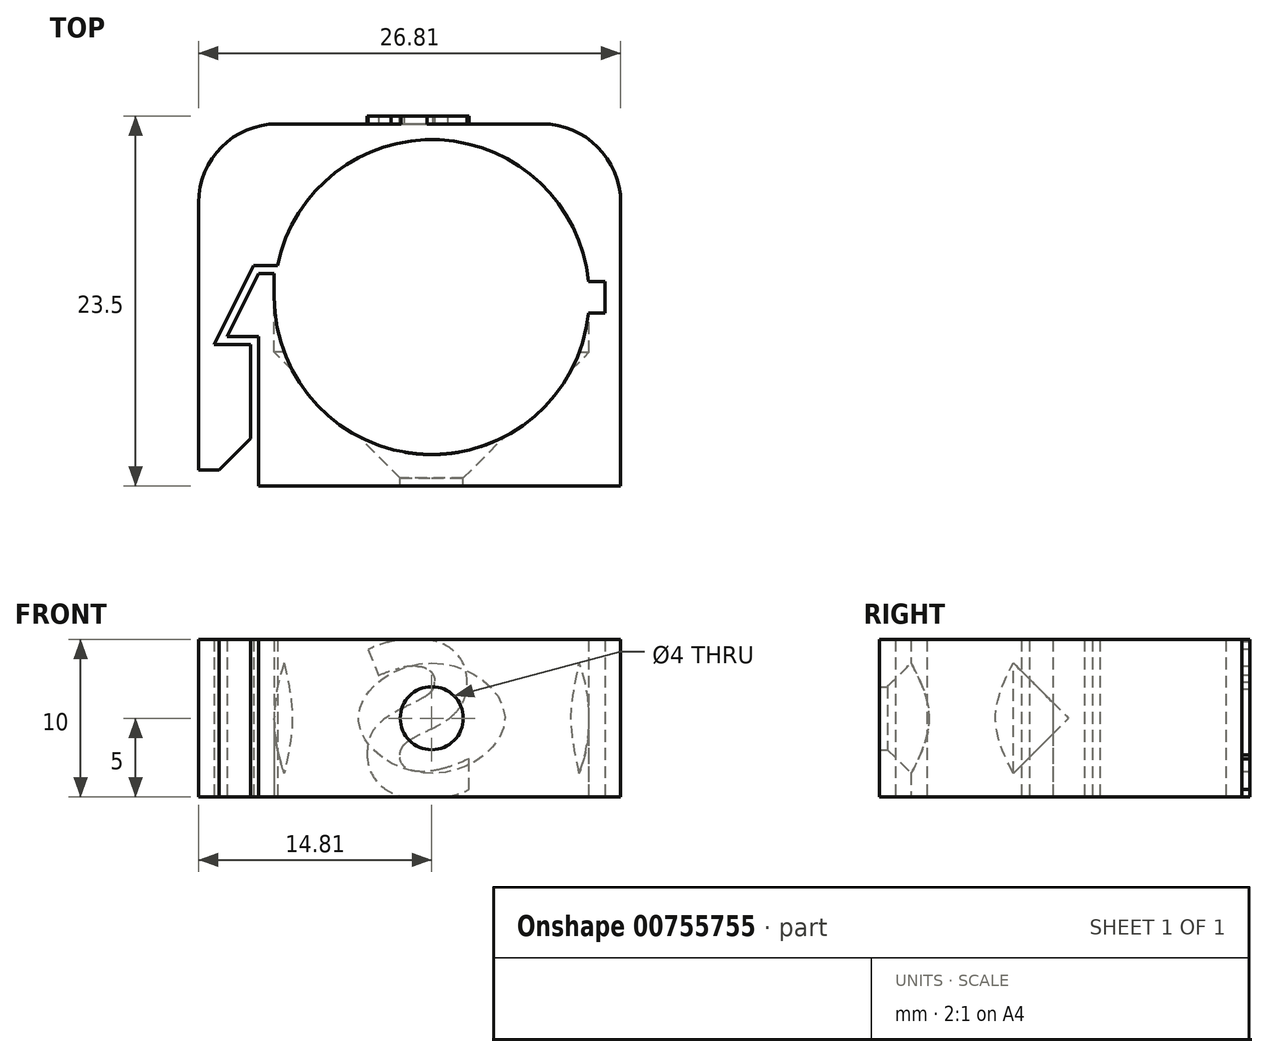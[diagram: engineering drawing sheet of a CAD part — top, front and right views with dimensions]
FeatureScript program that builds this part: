
annotation { "Feature Type Name" : "Feature", "Feature Type Description" : "" }
export const myFeature = defineFeature(function(context is Context, id is Id, definition is map)
    precondition{}
    {
        {
            var Q0;
            Q0=qCreatedBy(makeId("Top.planeOp"),FACE);
            var sketch = newSketch(context, id + "F0", { "sketchPlane" : qUnion([Q0])});
            skArc(sketch, "E0", {"start": v(-10, 0) * mm, "mid": v(9.95, -1) * mm, "end": v(-9.8, 2) * mm});
            skLineSegment(sketch, "E1", {"start": v(-11, 1.5) * mm, "end": v(-13, -2.5) * mm});
            skLineSegment(sketch, "E2", {"start": v(-13, -2.5) * mm, "end": v(-11, -2.5) * mm});
            skLineSegment(sketch, "E3", {"start": v(-11, -2.5) * mm, "end": v(-11, -12) * mm});
            skLineSegment(sketch, "E4", {"start": v(-11, -12) * mm, "end": v(12, -12) * mm});
            skLineSegment(sketch, "E5", {"start": v(12, -12) * mm, "end": v(12, 12) * mm});
            skCircle(sketch, "E6.0", {"center": v(0, 0) * mm, "radius": 12 * mm, "construction": true});
            skLineSegment(sketch, "E7", {"start": v(12, 12) * mm, "end": v(-14.8, 12) * mm});
            skLineSegment(sketch, "E8", {"start": v(-11, 1.5) * mm, "end": v(-10, 1.5) * mm});
            skLineSegment(sketch, "E9", {"start": v(-14.8, 12) * mm, "end": v(-14.8, -11) * mm});
            skLineSegment(sketch, "E10", {"start": v(-10, 1.5) * mm, "end": v(-10, 0) * mm});
            skLineSegment(sketch, "E11.0", {"start": v(-11.3, 2) * mm, "end": v(-9.8, 2) * mm});
            skLineSegment(sketch, "E11.1", {"start": v(-11.3, 2) * mm, "end": v(-13.8, -3) * mm});
            skLineSegment(sketch, "E12.0", {"start": v(-13.8, -3) * mm, "end": v(-11.5, -3) * mm});
            skLineSegment(sketch, "E13", {"start": v(-11.5, -3) * mm, "end": v(-11.5, -11) * mm});
            skLineSegment(sketch, "E14", {"start": v(-11.5, -11) * mm, "end": v(-14.8, -11) * mm});
            skPoint(sketch, "E15", {"position": v(-14.8, -5) * mm});
            skPoint(sketch, "E16", {"position": v(10, 0) * mm});
            skLineSegment(sketch, "E17.bottom", {"start": v(9, 1) * mm, "end": v(11, 1) * mm});
            skLineSegment(sketch, "E17.top", {"start": v(9, -1) * mm, "end": v(11, -1) * mm});
            skLineSegment(sketch, "E17.left", {"start": v(9, 1) * mm, "end": v(9, -1) * mm});
            skLineSegment(sketch, "E17.right", {"start": v(11, 1) * mm, "end": v(11, -1) * mm});
            skLineSegment(sketch, "E18", {"start": v(-14.8, 11) * mm, "end": v(12, 11) * mm});
            skPoint(sketch, "E19", {"position": v(0, 10) * mm});
            skPoint(sketch, "E20.orphan", {"position": v(-18.8, -1) * mm});
            skPoint(sketch, "E21.center.orphan", {"position": v(-14.8, -1) * mm});
            skSolve(sketch);
        }
        {
            var Q0;
            Q0=makeQuery(id+"F0.imprint","IMPRINT",FACE,{"disambiguationData":[TD([[makeQuery(id+"F0.imprint","IMPRINT",EDGE,{"derivedFrom":sQuery(id+"F0.wireOp",EDGE,"E1")}),1.0]])]});
            extrude(context, id + "F1", {"entities" : qUnion([Q0]), "depth" : 10 * mm, "offsetDistance" : 25 * mm, "symmetric" : true});
        }
        {
            var Q0;
            Q0=qCreatedBy(makeId("Top.planeOp"),FACE);
            var sketch = newSketch(context, id + "F2", { "sketchPlane" : qUnion([Q0])});
            skLineSegment(sketch, "E22", {"start": v(0, 0) * mm, "end": v(0, -12) * mm, "construction": true});
            skPoint(sketch, "E23", {"position": v(-10, 1.5) * mm});
            skLineSegment(sketch, "E24", {"start": v(-10, 1.5) * mm, "end": v(-10, -3.5) * mm});
            skLineSegment(sketch, "E25", {"start": v(-10, -3.5) * mm, "end": v(-2, -11.5) * mm});
            skLineSegment(sketch, "E26", {"start": v(-2, -11.5) * mm, "end": v(-2, -12) * mm});
            skLineSegment(sketch, "E27", {"start": v(-2, -12) * mm, "end": v(0, -12) * mm});
            skLineSegment(sketch, "E28", {"start": v(-10, 1.5) * mm, "end": v(0, 1.5) * mm});
            skLineSegment(sketch, "E29", {"start": v(0, 1.5) * mm, "end": v(0, -12) * mm});
            skLineSegment(sketch, "E30", {"start": v(0.13, 0) * mm, "end": v(-10, 0) * mm});
            skSolve(sketch);
        }
        {
            var Q0;
            {var subQ1=sQuery(id+"F2.wireOp",EDGE,"E25");Q0=makeQuery(id+"F2.imprint","IMPRINT",FACE,{"disambiguationData":[TD([[makeQuery(id+"F2.imprint","IMPRINT",EDGE,{"derivedFrom":subQ1}),1.0]])]});}
            var Q1;
            Q1=sQuery(id+"F2.wireOp",EDGE,"E29");
            revolve(context, id + "F3", {"operationType" : NewBodyOperationType.REMOVE, "surfaceOperationType" : NewSurfaceOperationType.NEW, "entities" : qUnion([Q0]), "axis" : qUnion([Q1]), "revolveType" : RevolveType.FULL});
        }
        {
            var Q0;
            Q0=makeQuery(id+"F1.opExtrude","SWEPT_EDGE",EDGE,{"disambiguationData":[OSD([sQuery(id+"F0.wireOp",EDGE,"E13"),sQuery(id+"F0.wireOp",EDGE,"E14")])]});
            chamfer(context, id + "F4", {"entities" : qUnion([Q0]), "width" : 2 * mm, "tangentPropagation" : true});
        }
        {
            var Q0;
            Q0=makeQuery(id+"F1.opExtrude","SWEPT_EDGE",EDGE,{"disambiguationData":[OSD([sQuery(id+"F0.wireOp",EDGE,"E5"),sQuery(id+"F0.wireOp",EDGE,"E18")])]});
            fillet(context, id + "F5", {"entities" : qUnion([Q0]), "radius" : 5 * mm, "tangentPropagation" : true, "allowEdgeOverflow" : false});
        }
        {
            var Q0;
            Q0=makeQuery(id+"F1.opExtrude","SWEPT_EDGE",EDGE,{"disambiguationData":[OSD([sQuery(id+"F0.wireOp",EDGE,"E9"),sQuery(id+"F0.wireOp",EDGE,"E18")])]});
            fillet(context, id + "F6", {"entities" : qUnion([Q0]), "radius" : 5 * mm, "tangentPropagation" : true, "allowEdgeOverflow" : false});
        }
        {
            var Q0;
            Q0=makeQuery(id+"F1.opExtrude","SWEPT_FACE",FACE,{"disambiguationData":[OSD([sQuery(id+"F0.wireOp",EDGE,"E18")])]});
            var sketch = newSketch(context, id + "F7", { "sketchPlane" : qUnion([Q0])});
            skText(sketch, "E31", { "text": "S", "fontName": "OpenSans-Bold.ttf"});
            const initialGuessF7  = {"E31": [-0.003, -0.005, 1, 0, 0.01]};
            skSetInitialGuess(sketch, initialGuessF7);
            skSolve(sketch);
        }
        {
            var Q0;
            {var subQ13=sQuery(id+"F7.wireOp",EDGE,"E31.sketch_text.stroke-0");Q0=makeQuery(id+"F7.imprint","IMPRINT",FACE,{"disambiguationData":[TD([[makeQuery(id+"F7.imprint","IMPRINT",EDGE,{"derivedFrom":subQ13}),-1.0]])]});}
            extrude(context, id + "F8", {"entities" : qUnion([Q0]), "operationType" : NewBodyOperationType.ADD, "depth" : 0.5 * mm, "offsetDistance" : 25 * mm});
        }
    });
